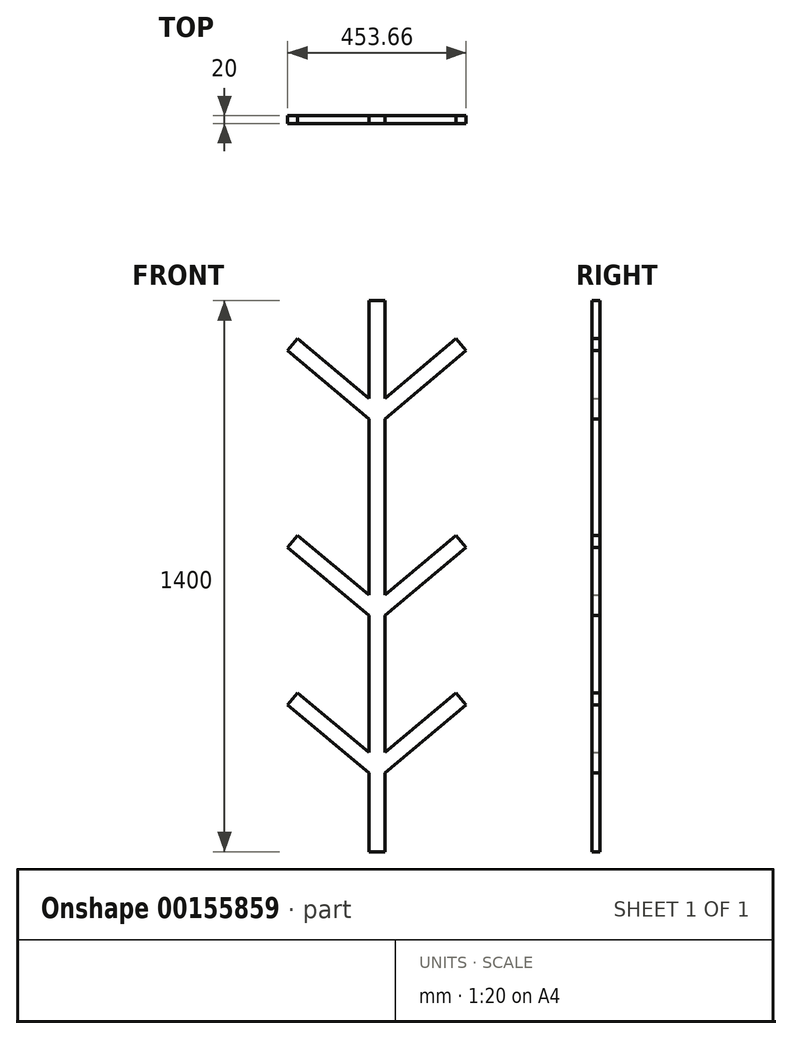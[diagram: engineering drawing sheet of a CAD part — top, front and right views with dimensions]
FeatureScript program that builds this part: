
annotation { "Feature Type Name" : "Feature", "Feature Type Description" : "" }
export const myFeature = defineFeature(function(context is Context, id is Id, definition is map)
    precondition{}
    {
        {
            var Q0;
            Q0=qCreatedBy(makeId("Front.planeOp"),FACE);
            var sketch = newSketch(context, id + "F0", { "sketchPlane" : qUnion([Q0])});
            skLineSegment(sketch, "E0.bottom", {"start": v(-52.1, 1140.97) * mm, "end": v(-12.1, 1140.97) * mm});
            skLineSegment(sketch, "E0.top", {"start": v(-52.1, -259.03) * mm, "end": v(-12.1, -259.03) * mm});
            skLineSegment(sketch, "E0.left", {"start": v(-52.1, 1140.97) * mm, "end": v(-52.1, -259.03) * mm});
            skLineSegment(sketch, "E0.right", {"start": v(-12.1, 1140.97) * mm, "end": v(-12.1, -259.03) * mm});
            skLineSegment(sketch, "E1", {"start": v(-52.1, 1140.97) * mm, "end": v(-52.1, 840.97) * mm});
            skLineSegment(sketch, "E2", {"start": v(-52.1, 840.97) * mm, "end": v(-258.92, 1014.52) * mm});
            skLineSegment(sketch, "E3", {"start": v(-258.92, 1014.52) * mm, "end": v(-233.21, 1045.16) * mm});
            skLineSegment(sketch, "E4", {"start": v(-233.21, 1045.16) * mm, "end": v(-52.1, 893.19) * mm});
            skLineSegment(sketch, "E5", {"start": v(-52.1, 893.19) * mm, "end": v(-52.1, 840.97) * mm});
            skLineSegment(sketch, "E6", {"start": v(-12.1, 1140.97) * mm, "end": v(-12.1, 840.97) * mm});
            skLineSegment(sketch, "E7", {"start": v(-12.1, 840.97) * mm, "end": v(194.74, 1014.52) * mm});
            skLineSegment(sketch, "E8", {"start": v(194.74, 1014.52) * mm, "end": v(169.03, 1045.16) * mm});
            skLineSegment(sketch, "E9", {"start": v(169.03, 1045.16) * mm, "end": v(-12.1, 893.19) * mm});
            skLineSegment(sketch, "E10", {"start": v(-12.1, 893.19) * mm, "end": v(-12.1, 840.97) * mm});
            skLineSegment(sketch, "E11", {"start": v(-52.1, 840.97) * mm, "end": v(-52.1, 340.97) * mm});
            skLineSegment(sketch, "E12", {"start": v(-52.1, 340.97) * mm, "end": v(-258.92, 514.52) * mm});
            skLineSegment(sketch, "E13", {"start": v(-258.92, 514.52) * mm, "end": v(-233.21, 545.16) * mm});
            skLineSegment(sketch, "E14", {"start": v(-233.21, 545.16) * mm, "end": v(-52.1, 393.19) * mm});
            skLineSegment(sketch, "E15", {"start": v(-12.1, 840.97) * mm, "end": v(-12.1, 340.97) * mm});
            skLineSegment(sketch, "E16", {"start": v(-12.1, 340.97) * mm, "end": v(194.74, 514.52) * mm});
            skLineSegment(sketch, "E17", {"start": v(194.74, 514.52) * mm, "end": v(169.03, 545.16) * mm});
            skLineSegment(sketch, "E18", {"start": v(169.03, 545.16) * mm, "end": v(-12.1, 393.19) * mm});
            skLineSegment(sketch, "E19", {"start": v(-52.1, 340.97) * mm, "end": v(-52.1, -59.03) * mm});
            skLineSegment(sketch, "E20", {"start": v(-52.1, -59.03) * mm, "end": v(-258.92, 114.52) * mm});
            skLineSegment(sketch, "E21", {"start": v(-258.92, 114.52) * mm, "end": v(-233.21, 145.16) * mm});
            skLineSegment(sketch, "E22", {"start": v(-233.21, 145.16) * mm, "end": v(-52.1, -6.81) * mm});
            skLineSegment(sketch, "E23", {"start": v(-12.1, 340.97) * mm, "end": v(-12.1, -59.03) * mm});
            skLineSegment(sketch, "E24", {"start": v(-12.1, -59.03) * mm, "end": v(194.74, 114.52) * mm});
            skLineSegment(sketch, "E25", {"start": v(194.74, 114.52) * mm, "end": v(169.03, 145.16) * mm});
            skLineSegment(sketch, "E26", {"start": v(169.03, 145.16) * mm, "end": v(-12.1, -6.81) * mm});
            skSolve(sketch);
        }
        {
            var Q0;
            Q0=makeQuery(id+"F0.imprint","IMPRINT",FACE,{"disambiguationData":[TD([[makeQuery(id+"F0.imprint","IMPRINT",EDGE,{"derivedFrom":sQuery(id+"F0.wireOp",EDGE,"E2")}),-1.0]])]});
            var Q1;
            Q1=makeQuery(id+"F0.imprint","IMPRINT",FACE,{"disambiguationData":[TD([[makeQuery(id+"F0.imprint","IMPRINT",EDGE,{"derivedFrom":sQuery(id+"F0.wireOp",EDGE,"E7")}),1.0]])]});
            var Q2;
            Q2=makeQuery(id+"F0.imprint","IMPRINT",FACE,{"disambiguationData":[TD([[makeQuery(id+"F0.imprint","IMPRINT",EDGE,{"derivedFrom":sQuery(id+"F0.wireOp",EDGE,"E0.bottom")}),-1.0]])]});
            var Q3;
            {var subQ0=sQuery(id+"F0.wireOp",EDGE,"E12");Q3=makeQuery(id+"F0.imprint","IMPRINT",FACE,{"disambiguationData":[TD([[makeQuery(id+"F0.imprint","IMPRINT",EDGE,{"derivedFrom":subQ0}),-1.0]])]});}
            var Q4;
            {var subQ0=sQuery(id+"F0.wireOp",EDGE,"E16");Q4=makeQuery(id+"F0.imprint","IMPRINT",FACE,{"disambiguationData":[TD([[makeQuery(id+"F0.imprint","IMPRINT",EDGE,{"derivedFrom":subQ0}),1.0]])]});}
            var Q5;
            {var subQ0=sQuery(id+"F0.wireOp",EDGE,"E20");Q5=makeQuery(id+"F0.imprint","IMPRINT",FACE,{"disambiguationData":[TD([[makeQuery(id+"F0.imprint","IMPRINT",EDGE,{"derivedFrom":subQ0}),-1.0]])]});}
            var Q6;
            {var subQ0=sQuery(id+"F0.wireOp",EDGE,"E24");Q6=makeQuery(id+"F0.imprint","IMPRINT",FACE,{"disambiguationData":[TD([[makeQuery(id+"F0.imprint","IMPRINT",EDGE,{"derivedFrom":subQ0}),1.0]])]});}
            extrude(context, id + "F1", {"entities" : qUnion([Q0, Q1, Q2, Q3, Q4, Q5, Q6]), "depth" : 20 * mm});
        }
    });
